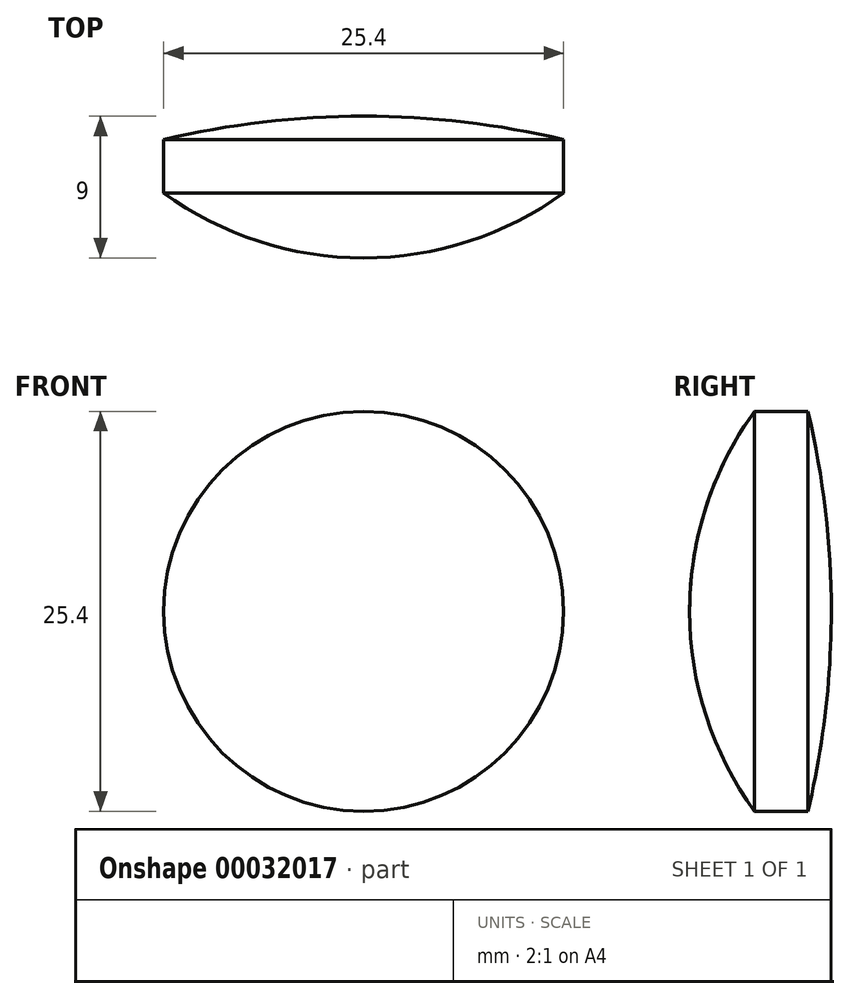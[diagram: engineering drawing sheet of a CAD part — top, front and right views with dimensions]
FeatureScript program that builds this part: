
annotation { "Feature Type Name" : "Feature", "Feature Type Description" : "" }
export const myFeature = defineFeature(function(context is Context, id is Id, definition is map)
    precondition{}
    {
        {
            var Q0;
            Q0=qCreatedBy(makeId("Right.planeOp"),FACE);
            var sketch = newSketch(context, id + "F0", { "sketchPlane" : qUnion([Q0])});
            skArc(sketch, "E0", {"start": v(0, 0) * mm, "mid": v(-0.37, 6.4) * mm, "end": v(-1.48, 12.7) * mm});
            skArc(sketch, "E1", {"start": v(-4.87, 12.7) * mm, "mid": v(-7.94, 6.68) * mm, "end": v(-9, 0) * mm});
            skLineSegment(sketch, "E2", {"start": v(-9, 0) * mm, "end": v(0, 0) * mm});
            skLineSegment(sketch, "E3", {"start": v(-4.87, 12.7) * mm, "end": v(-1.48, 12.7) * mm});
            skLineSegment(sketch, "E4", {"start": v(0, 0) * mm, "end": v(12.6, 0) * mm, "construction": true});
            skSolve(sketch);
        }
        {
            var Q0;
            Q0 = qSketchRegion(id + "F0", true);
            var Q1;
            Q1=sQuery(id+"F0.wireOp",EDGE,"E4");
            revolve(context, id + "F1", {"entities" : qUnion([Q0]), "axis" : qUnion([Q1]), "revolveType" : RevolveType.FULL});
        }
    });
